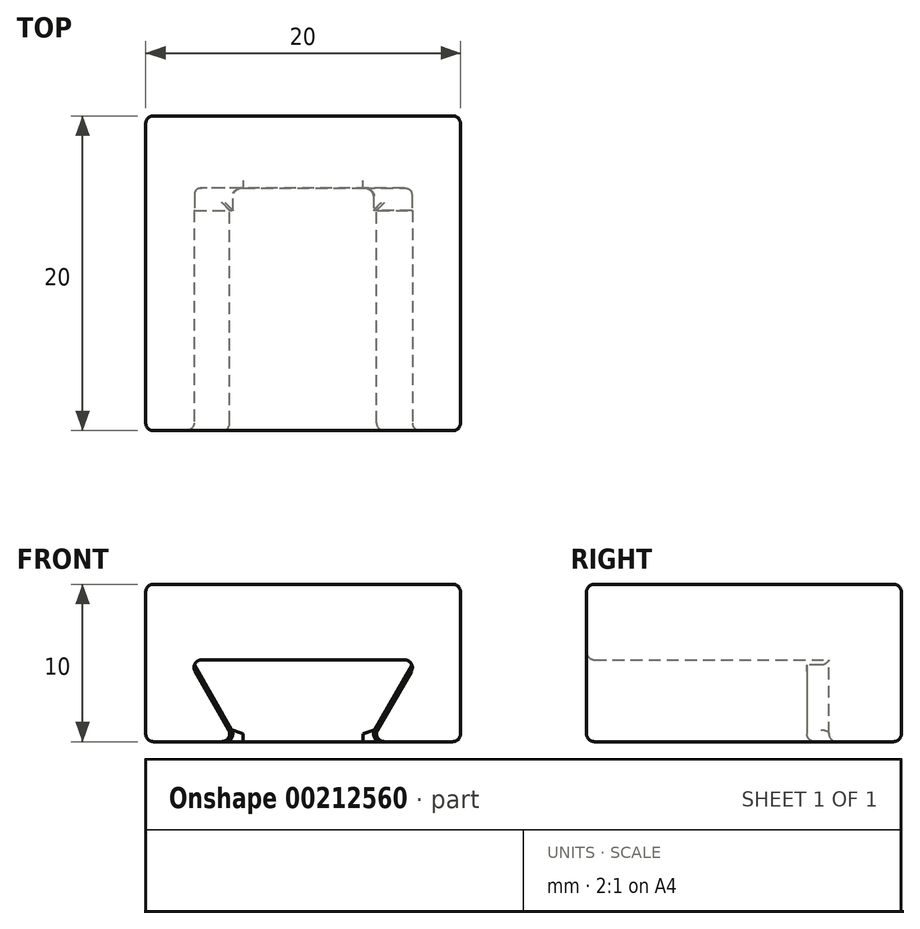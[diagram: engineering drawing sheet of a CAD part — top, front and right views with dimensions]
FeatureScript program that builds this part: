
annotation { "Feature Type Name" : "Feature", "Feature Type Description" : "" }
export const myFeature = defineFeature(function(context is Context, id is Id, definition is map)
    precondition{}
    {
        {
            var Q0;
            Q0=qCreatedBy(makeId("Front.planeOp"),FACE);
            var sketch = newSketch(context, id + "F0", { "sketchPlane" : qUnion([Q0])});
            skLineSegment(sketch, "E0", {"start": v(0, 0) * mm, "end": v(0, 10) * mm});
            skLineSegment(sketch, "E1", {"start": v(0, 10) * mm, "end": v(20, 10) * mm});
            skLineSegment(sketch, "E2", {"start": v(20, 10) * mm, "end": v(20, 0) * mm});
            skLineSegment(sketch, "E3", {"start": v(20, 0) * mm, "end": v(14.3, 0) * mm});
            skLineSegment(sketch, "E4", {"start": v(14.3, 0) * mm, "end": v(17.3, 5.2) * mm});
            skLineSegment(sketch, "E5", {"start": v(17.3, 5.2) * mm, "end": v(2.7, 5.2) * mm});
            skLineSegment(sketch, "E6", {"start": v(2.7, 5.2) * mm, "end": v(5.7, 0) * mm});
            skLineSegment(sketch, "E7", {"start": v(5.7, 0) * mm, "end": v(0, 0) * mm});
            skSolve(sketch);
        }
        {
            var Q0;
            Q0=makeQuery(id+"F0.imprint","IMPRINT",FACE,{"disambiguationData":[TD([[makeQuery(id+"F0.imprint","IMPRINT",EDGE,{"derivedFrom":sQuery(id+"F0.wireOp",EDGE,"E0")}),-1.0]])]});
            extrude(context, id + "F1", {"entities" : qUnion([Q0]), "depth" : 15.4 * mm});
        }
        {
            var Q0;
            Q0=makeQuery(id+"F1.opExtrude","CAP_FACE",FACE,{"disambiguationData":[OSD([sQuery(id+"F0.wireOp",EDGE,"E0"),sQuery(id+"F0.wireOp",EDGE,"E1"),sQuery(id+"F0.wireOp",EDGE,"E2"),sQuery(id+"F0.wireOp",EDGE,"E3"),sQuery(id+"F0.wireOp",EDGE,"E4"),sQuery(id+"F0.wireOp",EDGE,"E5"),sQuery(id+"F0.wireOp",EDGE,"E6"),sQuery(id+"F0.wireOp",EDGE,"E7")])],"isStart":true});
            var sketch = newSketch(context, id + "F2", { "sketchPlane" : qUnion([Q0])});
            skLineSegment(sketch, "E8.bottom", {"start": v(0, 0) * mm, "end": v(-20, 0) * mm});
            skLineSegment(sketch, "E8.top", {"start": v(0, 10) * mm, "end": v(-20, 10) * mm});
            skLineSegment(sketch, "E8.left", {"start": v(0, 0) * mm, "end": v(0, 10) * mm});
            skLineSegment(sketch, "E8.right", {"start": v(-20, 0) * mm, "end": v(-20, 10) * mm});
            skSolve(sketch);
        }
        {
            var Q0;
            Q0=qSketchRegion(id+"F2",true);
            extrude(context, id + "F3", {"entities" : qUnion([Q0]), "operationType" : NewBodyOperationType.ADD, "depth" : 4.6 * mm});
        }
        {
            var Q0;
            Q0=makeQuery(id+"F1.opExtrude","CAP_FACE",FACE,{"disambiguationData":[OSD([sQuery(id+"F0.wireOp",EDGE,"E0"),sQuery(id+"F0.wireOp",EDGE,"E1"),sQuery(id+"F0.wireOp",EDGE,"E2"),sQuery(id+"F0.wireOp",EDGE,"E3"),sQuery(id+"F0.wireOp",EDGE,"E4"),sQuery(id+"F0.wireOp",EDGE,"E5"),sQuery(id+"F0.wireOp",EDGE,"E6"),sQuery(id+"F0.wireOp",EDGE,"E7")])],"isStart":false});
            var sketch = newSketch(context, id + "F4", { "sketchPlane" : qUnion([Q0])});
            skLineSegment(sketch, "E9.0", {"start": v(14.3, 0) * mm, "end": v(17.3, 5.2) * mm});
            skLineSegment(sketch, "E9.1", {"start": v(2.7, 5.2) * mm, "end": v(5.7, 0) * mm});
            skLineSegment(sketch, "E10", {"start": v(2.9, 5.2) * mm, "end": v(5.9, 0) * mm});
            skLineSegment(sketch, "E11", {"start": v(5.9, 0) * mm, "end": v(5.7, 0) * mm});
            skLineSegment(sketch, "E12", {"start": v(2.7, 5.2) * mm, "end": v(2.9, 5.2) * mm});
            skLineSegment(sketch, "E13", {"start": v(17.1, 5.2) * mm, "end": v(14.1, 0) * mm});
            skLineSegment(sketch, "E14", {"start": v(14.3, 0) * mm, "end": v(14.1, 0) * mm});
            skLineSegment(sketch, "E15", {"start": v(17.1, 5.2) * mm, "end": v(17.3, 5.2) * mm});
            skSolve(sketch);
        }
        {
            var Q0;
            Q0 = qSketchRegion(id + "F4", true);
            extrude(context, id + "F5", {"entities" : qUnion([Q0]), "operationType" : NewBodyOperationType.ADD, "oppositeDirection" : true, "depth" : 16 * mm, "hasSecondDirection" : true, "secondDirectionOppositeDirection" : true, "secondDirectionDepth" : 14 * mm});
        }
        {
            var Q0;
            Q0=makeQuery(id+"F1.opExtrude","CAP_EDGE",EDGE,{"disambiguationData":[OSD([sQuery(id+"F0.wireOp",EDGE,"E0")])],"isStart":false});
            var Q1;
            Q1=makeQuery(id+"F1.opExtrude","CAP_EDGE",EDGE,{"disambiguationData":[OSD([sQuery(id+"F0.wireOp",EDGE,"E1")])],"isStart":false});
            var Q2;
            Q2=makeQuery(id+"F1.opExtrude","CAP_EDGE",EDGE,{"disambiguationData":[OSD([sQuery(id+"F0.wireOp",EDGE,"E2")])],"isStart":false});
            var Q3;
            Q3=makeQuery(id+"F1.opExtrude","CAP_EDGE",EDGE,{"disambiguationData":[OSD([sQuery(id+"F0.wireOp",EDGE,"E3")])],"isStart":false});
            var Q4;
            Q4=makeQuery(id+"F1.opExtrude","CAP_FACE",FACE,{"disambiguationData":[OSD([sQuery(id+"F0.wireOp",EDGE,"E0"),sQuery(id+"F0.wireOp",EDGE,"E1"),sQuery(id+"F0.wireOp",EDGE,"E2"),sQuery(id+"F0.wireOp",EDGE,"E3"),sQuery(id+"F0.wireOp",EDGE,"E4"),sQuery(id+"F0.wireOp",EDGE,"E5"),sQuery(id+"F0.wireOp",EDGE,"E6"),sQuery(id+"F0.wireOp",EDGE,"E7")])],"isStart":false});
            var Q5;
            Q5=makeQuery(id+"F3.boolean.opBoolean","MERGE",FACE,{"derivedFrom":[makeQuery(id+"F1.opExtrude","SWEPT_FACE",FACE,{"disambiguationData":[OSD([sQuery(id+"F0.wireOp",EDGE,"E2")])]}),makeQuery(id+"F3.opExtrude","SWEPT_FACE",FACE,{"disambiguationData":[OSD([sQuery(id+"F2.wireOp",EDGE,"E8.right")])]})]});
            var Q6;
            Q6=makeQuery(id+"F3.boolean.opBoolean","MERGE",FACE,{"derivedFrom":[makeQuery(id+"F1.opExtrude","SWEPT_FACE",FACE,{"disambiguationData":[OSD([sQuery(id+"F0.wireOp",EDGE,"E1")])]}),makeQuery(id+"F3.opExtrude","SWEPT_FACE",FACE,{"disambiguationData":[OSD([sQuery(id+"F2.wireOp",EDGE,"E8.top")])]})]});
            var Q7;
            Q7=makeQuery(id+"F3.boolean.opBoolean","MERGE",FACE,{"derivedFrom":[makeQuery(id+"F1.opExtrude","SWEPT_FACE",FACE,{"disambiguationData":[OSD([sQuery(id+"F0.wireOp",EDGE,"E0")])]}),makeQuery(id+"F3.opExtrude","SWEPT_FACE",FACE,{"disambiguationData":[OSD([sQuery(id+"F2.wireOp",EDGE,"E8.left")])]})]});
            var Q8;
            Q8=makeQuery(id+"F3.opExtrude","CAP_FACE",FACE,{"disambiguationData":[OSD([sQuery(id+"F2.wireOp",EDGE,"E8.bottom"),sQuery(id+"F2.wireOp",EDGE,"E8.top"),sQuery(id+"F2.wireOp",EDGE,"E8.left"),sQuery(id+"F2.wireOp",EDGE,"E8.right")])],"isStart":false});
            var Q9;
            Q9=makeQuery(id+"F5.boolean.opBoolean","MERGE",FACE,{"derivedFrom":[makeQuery(id+"F3.boolean.opBoolean","MERGE",FACE,{"derivedFrom":[makeQuery(id+"F1.opExtrude","SWEPT_FACE",FACE,{"disambiguationData":[OSD([sQuery(id+"F0.wireOp",EDGE,"E3")])]}),makeQuery(id+"F1.opExtrude","SWEPT_FACE",FACE,{"disambiguationData":[OSD([sQuery(id+"F0.wireOp",EDGE,"E7")])]}),makeQuery(id+"F3.opExtrude","SWEPT_FACE",FACE,{"disambiguationData":[OSD([sQuery(id+"F2.wireOp",EDGE,"E8.bottom")])]})]}),makeQuery(id+"F5.opExtrude","SWEPT_FACE",FACE,{"disambiguationData":[OSD([sQuery(id+"F4.wireOp",EDGE,"E11")])]}),makeQuery(id+"F5.opExtrude","SWEPT_FACE",FACE,{"disambiguationData":[OSD([sQuery(id+"F4.wireOp",EDGE,"E14")])]})]});
            var Q10;
            Q10=makeQuery(id+"F5.boolean.opBoolean","INTERSECT",EDGE,{"derivedFrom":[makeQuery(id+"F3.opExtrude","CAP_FACE",FACE,{"disambiguationData":[OSD([sQuery(id+"F2.wireOp",EDGE,"E8.bottom"),sQuery(id+"F2.wireOp",EDGE,"E8.top"),sQuery(id+"F2.wireOp",EDGE,"E8.left"),sQuery(id+"F2.wireOp",EDGE,"E8.right")])],"isStart":true}),makeQuery(id+"F5.opExtrude","SWEPT_FACE",FACE,{"disambiguationData":[OSD([sQuery(id+"F4.wireOp",EDGE,"E10")])]})]});
            var Q11;
            Q11=makeQuery(id+"F5.boolean.opBoolean","INTERSECT",EDGE,{"derivedFrom":[makeQuery(id+"F3.opExtrude","CAP_FACE",FACE,{"disambiguationData":[OSD([sQuery(id+"F2.wireOp",EDGE,"E8.bottom"),sQuery(id+"F2.wireOp",EDGE,"E8.top"),sQuery(id+"F2.wireOp",EDGE,"E8.left"),sQuery(id+"F2.wireOp",EDGE,"E8.right")])],"isStart":true}),makeQuery(id+"F5.opExtrude","SWEPT_FACE",FACE,{"disambiguationData":[OSD([sQuery(id+"F4.wireOp",EDGE,"E13")])]})]});
            var Q12;
            Q12=makeQuery(id+"F1.opExtrude","CAP_EDGE",EDGE,{"disambiguationData":[OSD([sQuery(id+"F0.wireOp",EDGE,"E5")])],"isStart":true});
            var Q13;
            Q13=makeQuery(id+"F1.opExtrude","SWEPT_EDGE",EDGE,{"disambiguationData":[OSD([sQuery(id+"F0.wireOp",EDGE,"E4"),sQuery(id+"F0.wireOp",EDGE,"E5")])]});
            var Q14;
            Q14=makeQuery(id+"F1.opExtrude","SWEPT_EDGE",EDGE,{"disambiguationData":[OSD([sQuery(id+"F0.wireOp",EDGE,"E5"),sQuery(id+"F0.wireOp",EDGE,"E6")])]});
            fillet(context, id + "F6", {"entities" : qUnion([Q0, Q1, Q2, Q3, Q4, Q5, Q6, Q7, Q8, Q9, Q10, Q11, Q12, Q13, Q14]), "radius" : 0.5 * mm, "tangentPropagation" : true, "allowEdgeOverflow" : false});
        }
    });
